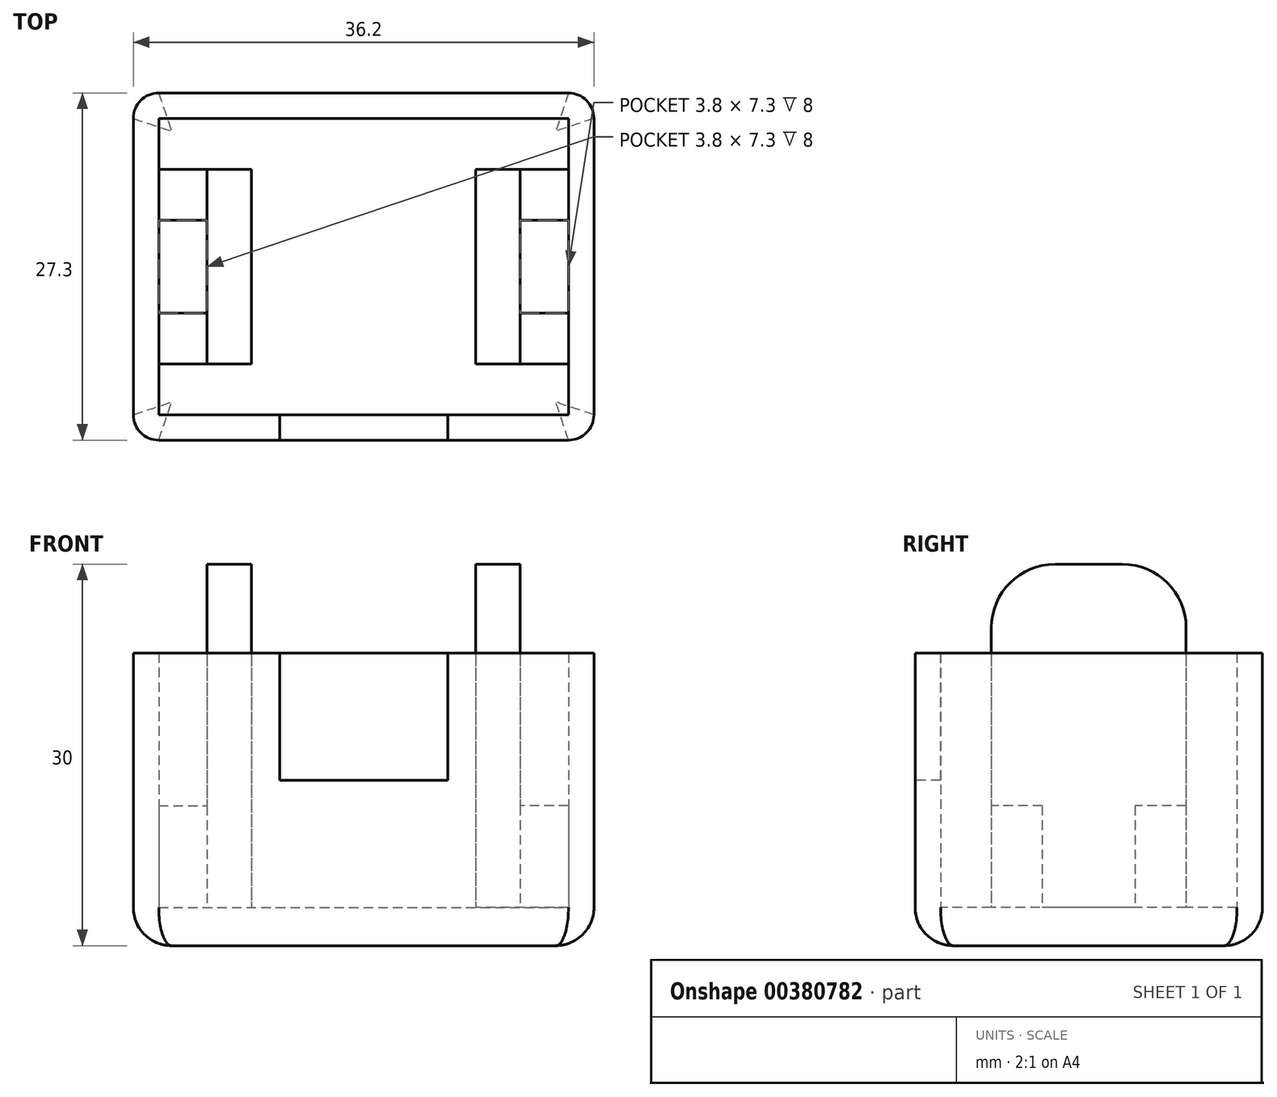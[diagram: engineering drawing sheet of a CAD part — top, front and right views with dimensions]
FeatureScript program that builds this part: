
annotation { "Feature Type Name" : "Feature", "Feature Type Description" : "" }
export const myFeature = defineFeature(function(context is Context, id is Id, definition is map)
    precondition{}
    {
        {
            var Q0;
            Q0=qCreatedBy(makeId("Top.planeOp"),FACE);
            var sketch = newSketch(context, id + "F0", { "sketchPlane" : qUnion([Q0])});
            skLineSegment(sketch, "E0.bottom", {"start": v(-18.66, 11.99) * mm, "end": v(17.54, 11.99) * mm});
            skLineSegment(sketch, "E0.top", {"start": v(-18.66, -15.31) * mm, "end": v(17.54, -15.31) * mm});
            skLineSegment(sketch, "E0.left", {"start": v(-18.66, 11.99) * mm, "end": v(-18.66, -15.31) * mm});
            skLineSegment(sketch, "E0.right", {"start": v(17.54, 11.99) * mm, "end": v(17.54, -15.31) * mm});
            skSolve(sketch);
        }
        {
            var Q0;
            Q0=qCreatedBy(makeId("Top.planeOp"),FACE);
            var sketch = newSketch(context, id + "F1", { "sketchPlane" : qUnion([Q0])});
            skLineSegment(sketch, "E1.bottom", {"start": v(-16.66, 9.99) * mm, "end": v(15.54, 9.99) * mm});
            skLineSegment(sketch, "E1.top", {"start": v(-16.66, -13.31) * mm, "end": v(15.54, -13.31) * mm});
            skLineSegment(sketch, "E1.left", {"start": v(-16.66, 9.99) * mm, "end": v(-16.66, -13.31) * mm});
            skLineSegment(sketch, "E1.right", {"start": v(15.54, 9.99) * mm, "end": v(15.54, -13.31) * mm});
            skSolve(sketch);
        }
        {
            var Q0;
            Q0 = qSketchRegion(id + "F0", true);
            extrude(context, id + "F2", {"entities" : qUnion([Q0]), "depth" : 20 * mm});
        }
        {
            var Q0;
            Q0 = qSketchRegion(id + "F1", true);
            extrude(context, id + "F3", {"entities" : qUnion([Q0]), "operationType" : NewBodyOperationType.REMOVE, "depth" : 20 * mm});
        }
        {
            var Q0;
            Q0=makeQuery(id+"F2.opExtrude","CAP_FACE",FACE,{"disambiguationData":[OSD([sQuery(id+"F0.wireOp",EDGE,"E0.bottom"),sQuery(id+"F0.wireOp",EDGE,"E0.top"),sQuery(id+"F0.wireOp",EDGE,"E0.left"),sQuery(id+"F0.wireOp",EDGE,"E0.right")])],"isStart":true});
            var sketch = newSketch(context, id + "F4", { "sketchPlane" : qUnion([Q0])});
            skLineSegment(sketch, "E2.bottom", {"start": v(-18.66, 15.31) * mm, "end": v(17.54, 15.31) * mm});
            skLineSegment(sketch, "E2.top", {"start": v(-18.66, -11.99) * mm, "end": v(17.54, -11.99) * mm});
            skLineSegment(sketch, "E2.left", {"start": v(-18.66, 15.31) * mm, "end": v(-18.66, -11.99) * mm});
            skLineSegment(sketch, "E2.right", {"start": v(17.54, 15.31) * mm, "end": v(17.54, -11.99) * mm});
            skSolve(sketch);
        }
        {
            var Q0;
            Q0 = qSketchRegion(id + "F4", true);
            extrude(context, id + "F5", {"entities" : qUnion([Q0]), "operationType" : NewBodyOperationType.ADD, "depth" : 3 * mm});
        }
        {
            var Q0;
            Q0=makeQuery(id+"F5.opExtrude","CAP_EDGE",EDGE,{"disambiguationData":[OSD([sQuery(id+"F4.wireOp",EDGE,"E2.top")])],"isStart":false});
            var Q1;
            Q1=makeQuery(id+"F5.opExtrude","CAP_EDGE",EDGE,{"disambiguationData":[OSD([sQuery(id+"F4.wireOp",EDGE,"E2.left")])],"isStart":false});
            var Q2;
            Q2=makeQuery(id+"F5.opExtrude","CAP_EDGE",EDGE,{"disambiguationData":[OSD([sQuery(id+"F4.wireOp",EDGE,"E2.bottom")])],"isStart":false});
            var Q3;
            Q3=makeQuery(id+"F5.opExtrude","CAP_EDGE",EDGE,{"disambiguationData":[OSD([sQuery(id+"F4.wireOp",EDGE,"E2.right")])],"isStart":false});
            fillet(context, id + "F6", {"entities" : qUnion([Q0, Q1, Q2, Q3]), "radius" : 3 * mm, "tangentPropagation" : true, "allowEdgeOverflow" : false});
        }
        {
            var Q0;
            Q0=makeQuery(id+"F6.opFillet","BLEND_EDGE",EDGE,{"blendedFrom":[makeQuery(id+"F5.opExtrude","CAP_EDGE",EDGE,{"disambiguationData":[OSD([sQuery(id+"F4.wireOp",EDGE,"E2.top")])],"isStart":false}),makeQuery(id+"F5.opExtrude","CAP_EDGE",EDGE,{"disambiguationData":[OSD([sQuery(id+"F4.wireOp",EDGE,"E2.right")])],"isStart":false})],"blendedInto":[]});
            var Q1;
            Q1=makeQuery(id+"F6.opFillet","BLEND_EDGE",EDGE,{"blendedFrom":[makeQuery(id+"F5.opExtrude","CAP_EDGE",EDGE,{"disambiguationData":[OSD([sQuery(id+"F4.wireOp",EDGE,"E2.bottom")])],"isStart":false}),makeQuery(id+"F5.opExtrude","CAP_EDGE",EDGE,{"disambiguationData":[OSD([sQuery(id+"F4.wireOp",EDGE,"E2.right")])],"isStart":false})],"blendedInto":[]});
            var Q2;
            Q2=makeQuery(id+"F6.opFillet","BLEND_EDGE",EDGE,{"blendedFrom":[makeQuery(id+"F5.opExtrude","CAP_EDGE",EDGE,{"disambiguationData":[OSD([sQuery(id+"F4.wireOp",EDGE,"E2.bottom")])],"isStart":false}),makeQuery(id+"F5.opExtrude","CAP_EDGE",EDGE,{"disambiguationData":[OSD([sQuery(id+"F4.wireOp",EDGE,"E2.left")])],"isStart":false})],"blendedInto":[]});
            var Q3;
            Q3=makeQuery(id+"F6.opFillet","BLEND_EDGE",EDGE,{"blendedFrom":[makeQuery(id+"F5.opExtrude","CAP_EDGE",EDGE,{"disambiguationData":[OSD([sQuery(id+"F4.wireOp",EDGE,"E2.top")])],"isStart":false}),makeQuery(id+"F5.opExtrude","CAP_EDGE",EDGE,{"disambiguationData":[OSD([sQuery(id+"F4.wireOp",EDGE,"E2.left")])],"isStart":false})],"blendedInto":[]});
            fillet(context, id + "F7", {"entities" : qUnion([Q0, Q1, Q2, Q3]), "radius" : 2 * mm, "tangentPropagation" : true, "allowEdgeOverflow" : false});
        }
        {
            var Q0;
            Q0=makeQuery(id+"F5.opExtrude","CAP_FACE",FACE,{"disambiguationData":[OSD([sQuery(id+"F4.wireOp",EDGE,"E2.bottom"),sQuery(id+"F4.wireOp",EDGE,"E2.top"),sQuery(id+"F4.wireOp",EDGE,"E2.left"),sQuery(id+"F4.wireOp",EDGE,"E2.right")])],"isStart":true});
            var sketch = newSketch(context, id + "F8", { "sketchPlane" : qUnion([Q0])});
            skLineSegment(sketch, "E3.bottom", {"start": v(-16.66, 5.99) * mm, "end": v(-12.86, 5.99) * mm});
            skLineSegment(sketch, "E3.top", {"start": v(-16.66, 1.99) * mm, "end": v(-12.86, 1.99) * mm});
            skLineSegment(sketch, "E3.left", {"start": v(-16.66, 5.99) * mm, "end": v(-16.66, 1.99) * mm});
            skLineSegment(sketch, "E3.right", {"start": v(-12.86, 5.99) * mm, "end": v(-12.86, 1.99) * mm});
            skLineSegment(sketch, "E4.bottom", {"start": v(-16.66, -9.31) * mm, "end": v(-12.86, -9.31) * mm});
            skLineSegment(sketch, "E4.top", {"start": v(-16.66, -5.31) * mm, "end": v(-12.86, -5.31) * mm});
            skLineSegment(sketch, "E4.left", {"start": v(-16.66, -9.31) * mm, "end": v(-16.66, -5.31) * mm});
            skLineSegment(sketch, "E4.right", {"start": v(-12.86, -9.31) * mm, "end": v(-12.86, -5.31) * mm});
            skLineSegment(sketch, "E5.bottom", {"start": v(15.54, 5.99) * mm, "end": v(11.74, 5.99) * mm});
            skLineSegment(sketch, "E5.top", {"start": v(15.54, 1.99) * mm, "end": v(11.74, 1.99) * mm});
            skLineSegment(sketch, "E5.left", {"start": v(15.54, 5.99) * mm, "end": v(15.54, 1.99) * mm});
            skLineSegment(sketch, "E5.right", {"start": v(11.74, 5.99) * mm, "end": v(11.74, 1.99) * mm});
            skLineSegment(sketch, "E6.bottom", {"start": v(15.54, -5.31) * mm, "end": v(11.74, -5.31) * mm});
            skLineSegment(sketch, "E6.top", {"start": v(15.54, -9.31) * mm, "end": v(11.74, -9.31) * mm});
            skLineSegment(sketch, "E6.left", {"start": v(15.54, -5.31) * mm, "end": v(15.54, -9.31) * mm});
            skLineSegment(sketch, "E6.right", {"start": v(11.74, -5.31) * mm, "end": v(11.74, -9.31) * mm});
            skSolve(sketch);
        }
        {
            var Q0;
            Q0 = qSketchRegion(id + "F8", true);
            extrude(context, id + "F9", {"entities" : qUnion([Q0]), "operationType" : NewBodyOperationType.ADD, "depth" : 8 * mm});
        }
        {
            var Q0;
            Q0=makeQuery(id+"F5.opExtrude","CAP_FACE",FACE,{"disambiguationData":[OSD([sQuery(id+"F4.wireOp",EDGE,"E2.bottom"),sQuery(id+"F4.wireOp",EDGE,"E2.top"),sQuery(id+"F4.wireOp",EDGE,"E2.left"),sQuery(id+"F4.wireOp",EDGE,"E2.right")])],"isStart":true});
            var sketch = newSketch(context, id + "F10", { "sketchPlane" : qUnion([Q0])});
            skLineSegment(sketch, "E7.bottom", {"start": v(-12.86, 5.99) * mm, "end": v(-9.36, 5.99) * mm});
            skLineSegment(sketch, "E7.top", {"start": v(-12.86, -9.31) * mm, "end": v(-9.36, -9.31) * mm});
            skLineSegment(sketch, "E7.left", {"start": v(-12.86, 5.99) * mm, "end": v(-12.86, -9.31) * mm});
            skLineSegment(sketch, "E7.right", {"start": v(-9.36, 5.99) * mm, "end": v(-9.36, -9.31) * mm});
            skLineSegment(sketch, "E8.bottom", {"start": v(11.74, 5.99) * mm, "end": v(8.24, 5.99) * mm});
            skLineSegment(sketch, "E8.top", {"start": v(11.74, -9.31) * mm, "end": v(8.24, -9.31) * mm});
            skLineSegment(sketch, "E8.left", {"start": v(11.74, 5.99) * mm, "end": v(11.74, -9.31) * mm});
            skLineSegment(sketch, "E8.right", {"start": v(8.24, 5.99) * mm, "end": v(8.24, -9.31) * mm});
            skSolve(sketch);
        }
        {
            var Q0;
            Q0 = qSketchRegion(id + "F10", true);
            extrude(context, id + "F11", {"entities" : qUnion([Q0]), "operationType" : NewBodyOperationType.ADD, "depth" : 27 * mm});
        }
        {
            var Q0;
            Q0=makeQuery(id+"F11.opExtrude","CAP_EDGE",EDGE,{"disambiguationData":[OSD([sQuery(id+"F10.wireOp",EDGE,"E7.top")])],"isStart":false});
            var Q1;
            Q1=makeQuery(id+"F11.opExtrude","CAP_EDGE",EDGE,{"disambiguationData":[OSD([sQuery(id+"F10.wireOp",EDGE,"E7.bottom")])],"isStart":false});
            var Q2;
            Q2=makeQuery(id+"F11.opExtrude","CAP_EDGE",EDGE,{"disambiguationData":[OSD([sQuery(id+"F10.wireOp",EDGE,"E8.bottom")])],"isStart":false});
            var Q3;
            Q3=makeQuery(id+"F11.opExtrude","CAP_EDGE",EDGE,{"disambiguationData":[OSD([sQuery(id+"F10.wireOp",EDGE,"E8.top")])],"isStart":false});
            fillet(context, id + "F12", {"entities" : qUnion([Q0, Q1, Q2, Q3]), "radius" : 5 * mm, "tangentPropagation" : true, "allowEdgeOverflow" : false});
        }
        {
            var Q0;
            Q0=makeQuery(id+"F5.boolean.opBoolean","MERGE",FACE,{"derivedFrom":[makeQuery(id+"F2.opExtrude","SWEPT_FACE",FACE,{"disambiguationData":[OSD([sQuery(id+"F0.wireOp",EDGE,"E0.top")])]}),makeQuery(id+"F5.opExtrude","SWEPT_FACE",FACE,{"disambiguationData":[OSD([sQuery(id+"F4.wireOp",EDGE,"E2.bottom")])]})]});
            var sketch = newSketch(context, id + "F13", { "sketchPlane" : qUnion([Q0])});
            skLineSegment(sketch, "E9.bottom", {"start": v(-7.16, 20) * mm, "end": v(6.04, 20) * mm});
            skLineSegment(sketch, "E9.top", {"start": v(-7.16, 10) * mm, "end": v(6.04, 10) * mm});
            skLineSegment(sketch, "E9.left", {"start": v(-7.16, 20) * mm, "end": v(-7.16, 10) * mm});
            skLineSegment(sketch, "E9.right", {"start": v(6.04, 20) * mm, "end": v(6.04, 10) * mm});
            skSolve(sketch);
        }
        {
            var Q0;
            Q0 = qSketchRegion(id + "F13", true);
            extrude(context, id + "F14", {"entities" : qUnion([Q0]), "operationType" : NewBodyOperationType.REMOVE, "oppositeDirection" : true, "depth" : 2.1 * mm});
        }
    });
